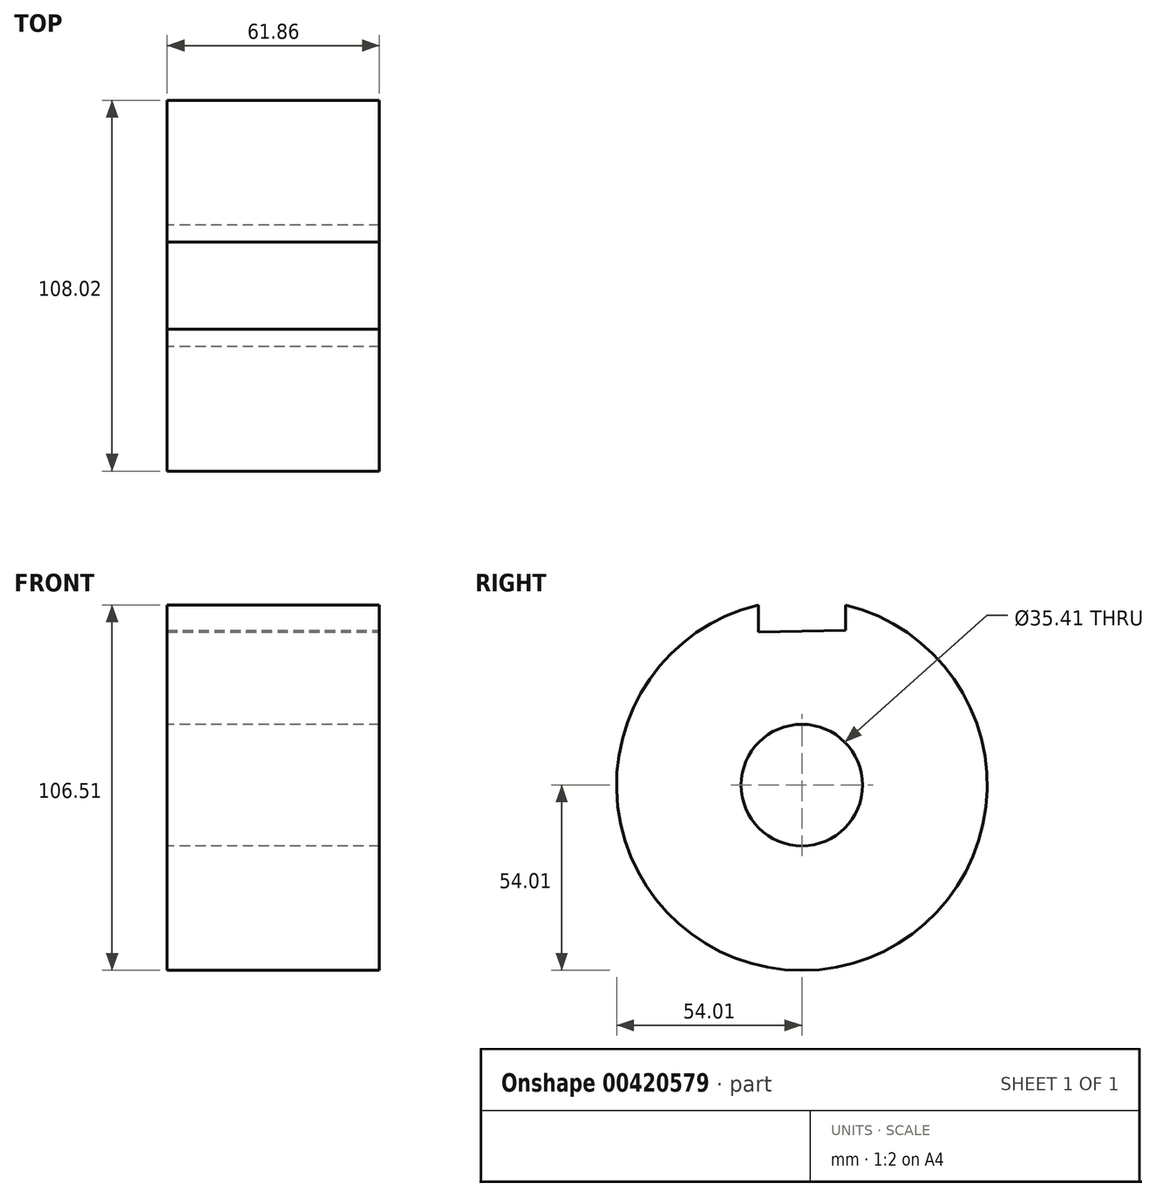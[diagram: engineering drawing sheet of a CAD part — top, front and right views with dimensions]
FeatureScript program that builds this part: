
annotation { "Feature Type Name" : "Feature", "Feature Type Description" : "" }
export const myFeature = defineFeature(function(context is Context, id is Id, definition is map)
    precondition{}
    {
        {
            var Q0;
            Q0=qCreatedBy(makeId("Front.planeOp"),FACE);
            var sketch = newSketch(context, id + "F0", { "sketchPlane" : qUnion([Q0])});
            skLineSegment(sketch, "E0", {"start": v(-171.23, 0) * mm, "end": v(87.4, 0) * mm, "construction": true});
            skLineSegment(sketch, "E1", {"start": v(0, 17.7) * mm, "end": v(61.86, 17.7) * mm});
            skLineSegment(sketch, "E2", {"start": v(61.86, 17.26) * mm, "end": v(61.86, 54.01) * mm});
            skLineSegment(sketch, "E3", {"start": v(61.86, 54.01) * mm, "end": v(0, 54.01) * mm});
            skLineSegment(sketch, "E4", {"start": v(0, 54.01) * mm, "end": v(0, 17.7) * mm});
            skSolve(sketch);
        }
        {
            var Q0;
            {var subQ0=sQuery(id+"F0.wireOp",EDGE,"E1");Q0=makeQuery(id+"F0.imprint","IMPRINT",FACE,{"disambiguationData":[TD([[makeQuery(id+"F0.imprint","IMPRINT",EDGE,{"derivedFrom":subQ0}),1.0]])]});}
            var Q1;
            Q1=sQuery(id+"F0.wireOp",EDGE,"E0");
            revolve(context, id + "F1", {"entities" : qUnion([Q0]), "axis" : qUnion([Q1]), "revolveType" : RevolveType.FULL});
        }
        {
            var Q0;
            Q0=makeQuery(id+"F1.opRevolve","SWEPT_FACE",FACE,{"disambiguationData":[OSD([sQuery(id+"F0.wireOp",EDGE,"E2")])]});
            var sketch = newSketch(context, id + "F2", { "sketchPlane" : qUnion([Q0])});
            skLineSegment(sketch, "E5", {"start": v(-12.7, 52.5) * mm, "end": v(-12.7, 44.6) * mm});
            skLineSegment(sketch, "E6", {"start": v(12.7, 45.05) * mm, "end": v(12.7, 52.5) * mm});
            skLineSegment(sketch, "E7", {"start": v(-12.7, 44.6) * mm, "end": v(12.7, 45.05) * mm});
            skSolve(sketch);
        }
        {
            var Q0;
            {var subQ0=sQuery(id+"F2.wireOp",EDGE,"E5");Q0=makeQuery(id+"F2.imprint","IMPRINT",FACE,{"disambiguationData":[TD([[makeQuery(id+"F2.imprint","IMPRINT",EDGE,{"derivedFrom":subQ0}),1.0]])]});}
            extrude(context, id + "F3", {"entities" : qUnion([Q0]), "operationType" : NewBodyOperationType.REMOVE, "endBound" : BoundingType.THROUGH_ALL, "oppositeDirection" : true, "depth" : 25.4 * mm});
        }
    });
